# Revit family: Shower_Wall_Abey_BuildersShowers_Horizontal_FaceBased
name_source: partatom
category: Plumbing Fixtures
units: mm (PartAtom-declared; Revit-internal decimal feet)

## family parameters
Cut with Voids When Loaded = Yes
Host = Face
Maintain Annotation Orientation = No
OmniClass Number = 23.31.17.00
OmniClass Title = Showers
Part Type = Normal
Room Calculation Point = No
Round Connector Dimension = Use Diameter
Shared = No

## types (3) — shared parameters
Assembly Code = D2010710
CW Connection = Yes
Default Elevation = 2,400 mm
HW Connection = Yes
IfcExportAs = IfcSanitaryTerminal
IfcExportType = SHOWER
Manufacturer = Abey
ManufacturerOverallDepth = 514 mm
ManufacturerOverallHeight = 135 mm
ManufacturerOverallWidth = 250 mm
ManufacturerURLProductSpecific = https://www.abeyspecifier.com.au
ModifiedIssue = 20251103 $
URL = https://www.abey.com.au
Uniclass2015Code = Pr_40_20_87_76
Uniclass2015Title = Shower heads
Uniclass2015Version = Products v1.38
Vent Connection = No
Waste Connection = No
zero-valued in all types: Cost

## per-type parameters (varying)
| type | Description | ManufacturerSpecCode | Material | Model | Type Comments |
| Chrome (1AB-SH + 1AB-HSA) | Abey Builders 304 Stainless Steel Horizontal Shower Head & Arm Chrome | 1AB-SH + 1AB-HSA | Metal_Abey_Chrome | 1AB-SH + 1AB-HSA | Shower - Wall - Horizontal - Chrome |
| Brushed Nickel (1AB-SH-BN + 1AB-HSA-BN) | Abey Builders 304 Stainless Steel Horizontal Shower Head & Arm Brushed Nickel | 1AB-SH-BN + 1AB-HSA-BN | Metal_Abey_BrushedNickel | 1AB-SH-BN + 1AB-HSA-BN | Shower - Wall - Horizontal - Brushed Nickel |
| Black (1AB-SH-B + 1AB-HSA-B) | Abey Builders 304 Stainless Steel Horizontal Shower Head & Arm Black | 1AB-SH-B + 1AB-HSA-B | Metal_Abey_Black | 1AB-SH-B + 1AB-HSA-B | Shower - Wall - Horizontal - Black |

## geometry (parser evidence)
native form markers: Sweep x5
no freeform markers — native parametric forms only
